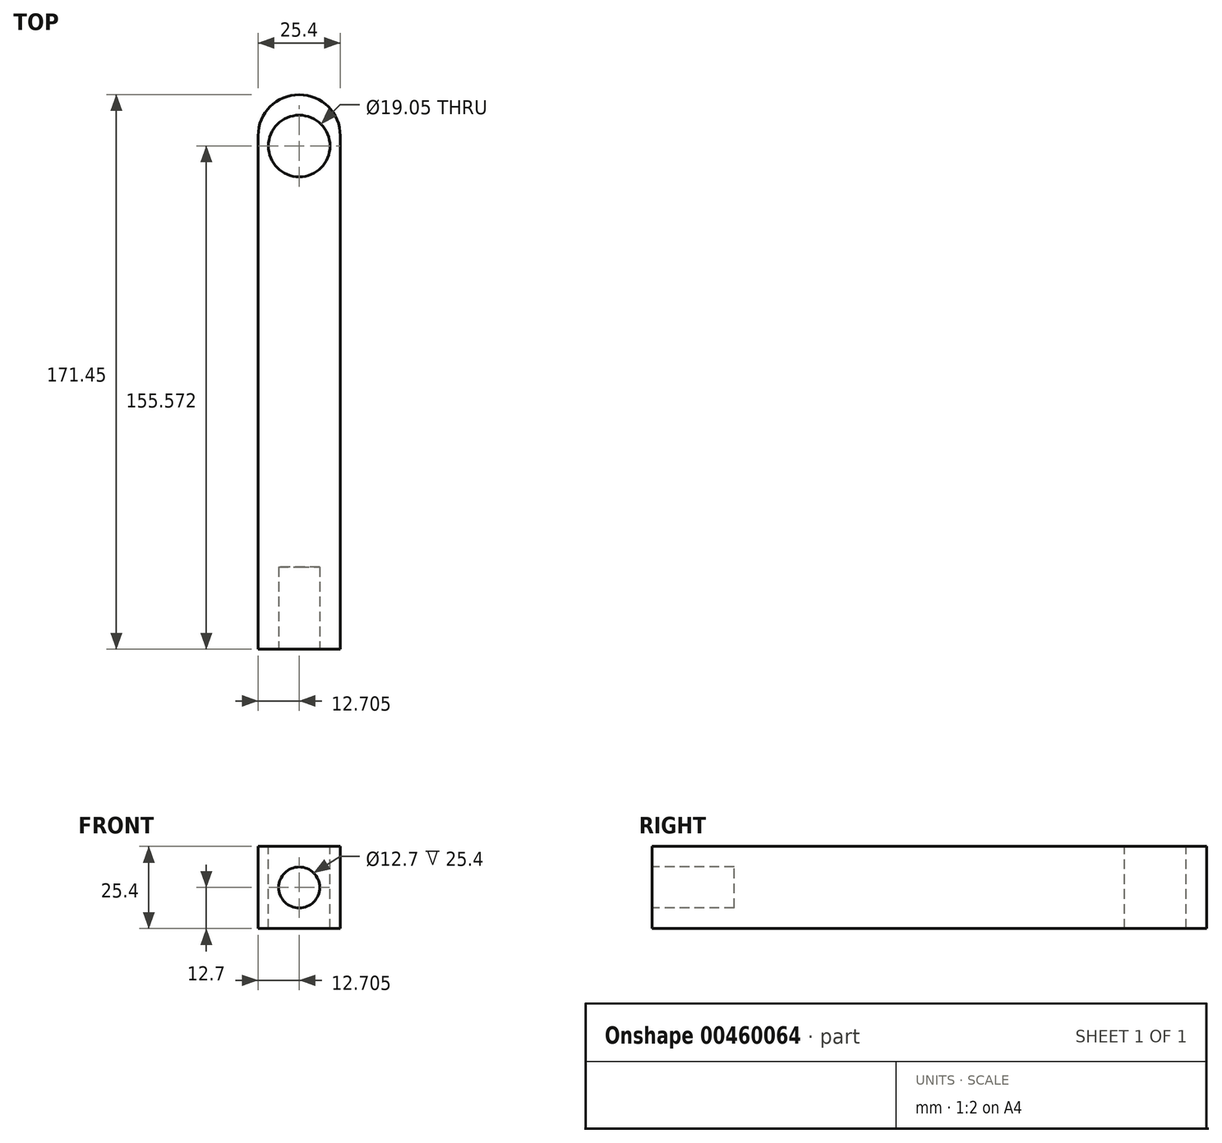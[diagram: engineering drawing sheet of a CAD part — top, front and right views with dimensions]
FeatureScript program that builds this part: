
annotation { "Feature Type Name" : "Feature", "Feature Type Description" : "" }
export const myFeature = defineFeature(function(context is Context, id is Id, definition is map)
    precondition{}
    {
        {
            var Q0;
            Q0=qCreatedBy(makeId("Top.planeOp"),FACE);
            var sketch = newSketch(context, id + "F0", { "sketchPlane" : qUnion([Q0])});
            skLineSegment(sketch, "E0.top", {"start": v(-45.9, 57.9) * mm, "end": v(-20.5, 57.9) * mm});
            skLineSegment(sketch, "E1", {"start": v(-20.5, 57.9) * mm, "end": v(-20.5, -113.54) * mm});
            skLineSegment(sketch, "E2", {"start": v(-20.5, -113.54) * mm, "end": v(-45.9, -113.54) * mm});
            skLineSegment(sketch, "E3", {"start": v(-45.9, -113.54) * mm, "end": v(-45.9, 57.9) * mm});
            skPoint(sketch, "E4.center.orphan", {"position": v(-20.5, -126.24) * mm});
            skCircle(sketch, "E5", {"center": v(-33.2, 42.03) * mm, "radius": 9.53 * mm});
            skPoint(sketch, "E5.centerSnap0", {"position": v(-33.2, 57.9) * mm});
            skPoint(sketch, "E6.trimOffspring.end.orphan", {"position": v(-20.5, -138.94) * mm});
            skSolve(sketch);
        }
        {
            var Q0;
            Q0=makeQuery(id+"F0.imprint","IMPRINT",FACE,{"disambiguationData":[TD([[makeQuery(id+"F0.imprint","IMPRINT",EDGE,{"derivedFrom":sQuery(id+"F0.wireOp",EDGE,"E0.top")}),-1.0]])]});
            var Q1;
            Q1=makeQuery(id+"F0.imprint","IMPRINT",FACE,{"disambiguationData":[TD([[makeQuery(id+"F0.imprint","IMPRINT",EDGE,{"derivedFrom":sQuery(id+"F0.wireOp",EDGE,"E2")}),1.0]])]});
            extrude(context, id + "F1", {"entities" : qUnion([Q0, Q1]), "oppositeDirection" : true, "depth" : 25.4 * mm});
        }
        {
            var Q0;
            Q0=makeQuery(id+"F1.opExtrude","SWEPT_EDGE",EDGE,{"disambiguationData":[OSD([sQuery(id+"F0.wireOp",EDGE,"E0.top"),sQuery(id+"F0.wireOp",EDGE,"E3")])]});
            var Q1;
            Q1=makeQuery(id+"F1.opExtrude","SWEPT_EDGE",EDGE,{"disambiguationData":[OSD([sQuery(id+"F0.wireOp",EDGE,"E0.top"),sQuery(id+"F0.wireOp",EDGE,"E1")])]});
            fillet(context, id + "F2", {"entities" : qUnion([Q0, Q1]), "radius" : 12.7 * mm, "tangentPropagation" : true, "allowEdgeOverflow" : false});
        }
        {
            var Q0;
            Q0=makeQuery(id+"F1.opExtrude","SWEPT_FACE",FACE,{"disambiguationData":[OSD([sQuery(id+"F0.wireOp",EDGE,"E2")])]});
            var sketch = newSketch(context, id + "F3", { "sketchPlane" : qUnion([Q0])});
            skCircle(sketch, "E7", {"center": v(-33.2, -12.7) * mm, "radius": 6.35 * mm});
            skPoint(sketch, "E7.centerSnap0", {"position": v(-33.2, 0) * mm});
            skPoint(sketch, "E8", {"position": v(-20.5, -12.7) * mm});
            skSolve(sketch);
        }
        {
            var Q0;
            Q0=makeQuery(id+"F3.imprint","IMPRINT",FACE,{"disambiguationData":[TD([[makeQuery(id+"F3.imprint","IMPRINT",EDGE,{"derivedFrom":sQuery(id+"F3.wireOp",EDGE,"E7")}),1.0]])]});
            extrude(context, id + "F4", {"entities" : qUnion([Q0]), "operationType" : NewBodyOperationType.REMOVE, "oppositeDirection" : true, "depth" : 25.4 * mm});
        }
    });
